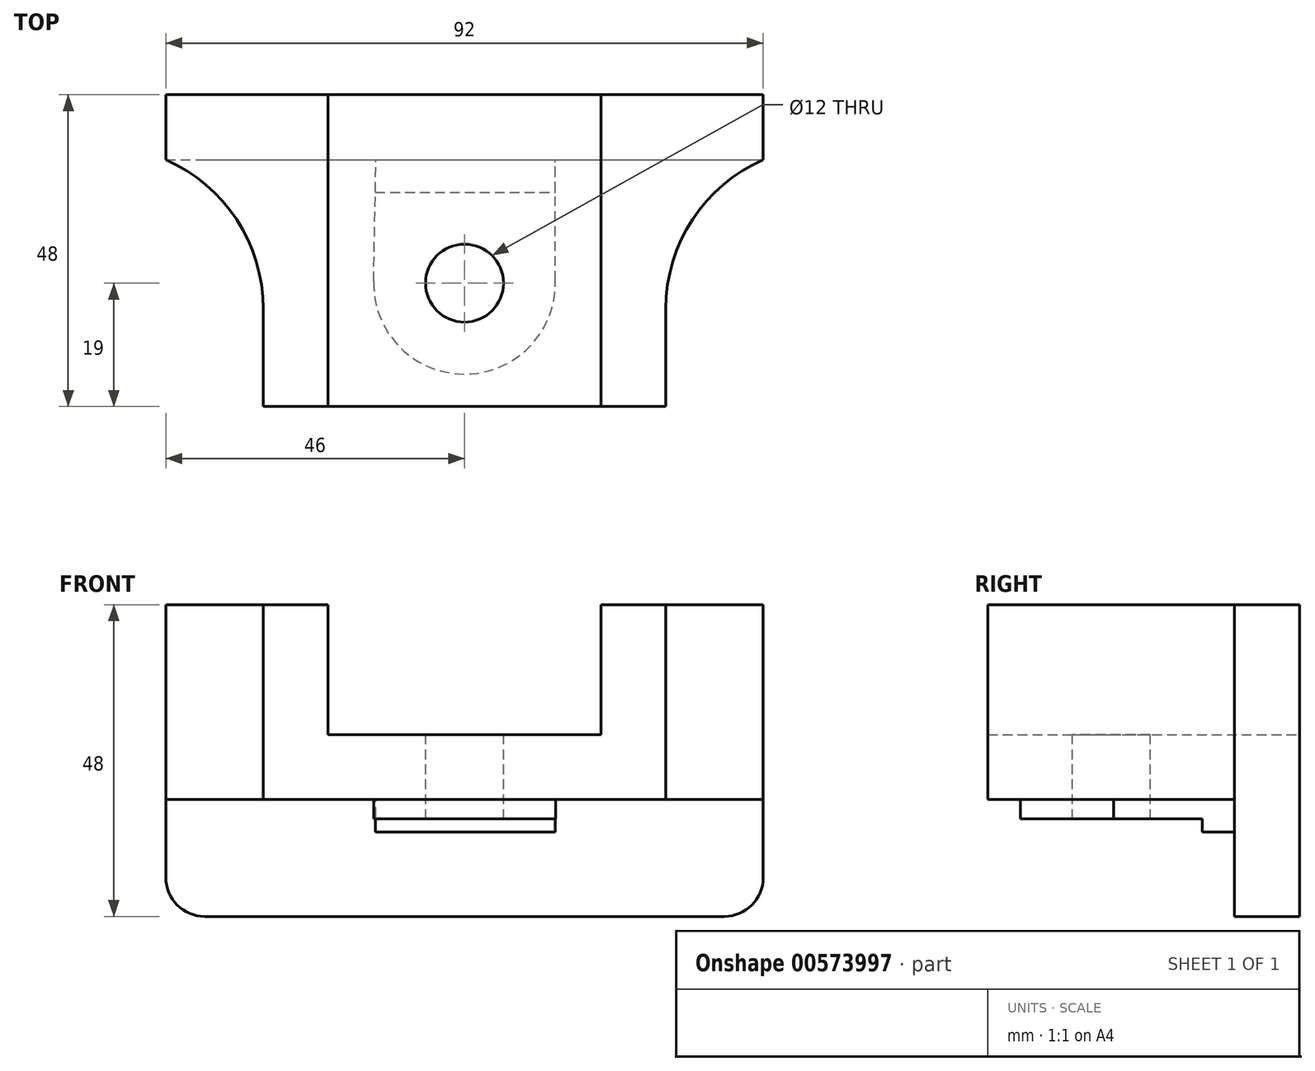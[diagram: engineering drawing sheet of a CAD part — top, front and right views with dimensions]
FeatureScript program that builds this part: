
annotation { "Feature Type Name" : "Feature", "Feature Type Description" : "" }
export const myFeature = defineFeature(function(context is Context, id is Id, definition is map)
    precondition{}
    {
        {
            var Q0;
            Q0=qCreatedBy(makeId("Front.planeOp"),FACE);
            var sketch = newSketch(context, id + "F0", { "sketchPlane" : qUnion([Q0])});
            skLineSegment(sketch, "E0", {"start": v(-46, 0) * mm, "end": v(-46, -42) * mm});
            skLineSegment(sketch, "E1", {"start": v(-40, -48) * mm, "end": v(40, -48) * mm});
            skLineSegment(sketch, "E2", {"start": v(46, -42) * mm, "end": v(46, 0) * mm});
            skLineSegment(sketch, "E3", {"start": v(46, 0) * mm, "end": v(21, 0) * mm});
            skLineSegment(sketch, "E4", {"start": v(21, 0) * mm, "end": v(21, -20) * mm});
            skLineSegment(sketch, "E5", {"start": v(21, -20) * mm, "end": v(-21, -20) * mm});
            skLineSegment(sketch, "E6", {"start": v(-21, -20) * mm, "end": v(-21, 0) * mm});
            skLineSegment(sketch, "E7", {"start": v(-21, 0) * mm, "end": v(-46, 0) * mm});
            skLineSegment(sketch, "E8", {"start": v(-31, 0) * mm, "end": v(-31, -30) * mm});
            skLineSegment(sketch, "E9", {"start": v(-31, -30) * mm, "end": v(31, -30) * mm});
            skLineSegment(sketch, "E10", {"start": v(31, -30) * mm, "end": v(31, 0) * mm});
            skPoint(sketch, "E11.visualSharp", {"position": v(-46, -48) * mm});
            skArc(sketch, "E11.filletArc", {"start": v(-46, -42) * mm, "mid": v(-44.24, -46.24) * mm, "end": v(-40, -48) * mm});
            skPoint(sketch, "E12.visualSharp", {"position": v(46, -48) * mm});
            skArc(sketch, "E12.filletArc", {"start": v(40, -48) * mm, "mid": v(44.24, -46.24) * mm, "end": v(46, -42) * mm});
            skSolve(sketch);
        }
        {
            var Q0;
            {var subQ1=sQuery(id+"F0.wireOp",EDGE,"E4");Q0=makeQuery(id+"F0.imprint","IMPRINT",FACE,{"disambiguationData":[TD([[makeQuery(id+"F0.imprint","IMPRINT",EDGE,{"derivedFrom":subQ1}),1.0]])]});}
            extrude(context, id + "F1", {"entities" : qUnion([Q0]), "depth" : 48 * mm, "offsetDistance" : 25 * mm});
        }
        {
            var Q0;
            Q0 = qSketchRegion(id + "F0", true);
            extrude(context, id + "F2", {"entities" : qUnion([Q0]), "operationType" : NewBodyOperationType.ADD, "depth" : 10 * mm, "offsetDistance" : 25 * mm});
        }
        {
            var Q0;
            Q0=makeQuery(id+"F1.opExtrude","SWEPT_FACE",FACE,{"disambiguationData":[OSD([sQuery(id+"F0.wireOp",EDGE,"E9")])]});
            var sketch = newSketch(context, id + "F3", { "sketchPlane" : qUnion([Q0])});
            skCircle(sketch, "E13", {"center": v(0, 29) * mm, "radius": 6 * mm});
            skArc(sketch, "E14", {"start": v(14, 28.65) * mm, "mid": v(0.04, 43) * mm, "end": v(-14, 28.73) * mm});
            skLineSegment(sketch, "E15", {"start": v(-14, 28.73) * mm, "end": v(-13.64, 10) * mm});
            skLineSegment(sketch, "E16", {"start": v(14, 28.65) * mm, "end": v(14, 10) * mm});
            skLineSegment(sketch, "E17", {"start": v(-13.73, 15) * mm, "end": v(14, 15) * mm});
            skSolve(sketch);
        }
        {
            var Q0;
            Q0=makeQuery(id+"F3.imprint","IMPRINT",FACE,{"disambiguationData":[TD([[makeQuery(id+"F3.imprint","IMPRINT",EDGE,{"derivedFrom":sQuery(id+"F3.wireOp",EDGE,"E13")}),-1.0]])]});
            extrude(context, id + "F4", {"entities" : qUnion([Q0]), "operationType" : NewBodyOperationType.ADD, "depth" : 3 * mm, "offsetDistance" : 25 * mm});
        }
        {
            var Q0;
            {var subQ3=sQuery(id+"F3.wireOp",EDGE,"E17");Q0=makeQuery(id+"F3.imprint","IMPRINT",FACE,{"disambiguationData":[TD([[makeQuery(id+"F3.imprint","IMPRINT",EDGE,{"derivedFrom":subQ3}),-1.0]])]});}
            extrude(context, id + "F5", {"entities" : qUnion([Q0]), "operationType" : NewBodyOperationType.ADD, "depth" : 5 * mm, "offsetDistance" : 25 * mm});
        }
        {
            var Q0;
            Q0=makeQuery(id+"F2.boolean.opBoolean","INTERSECT",EDGE,{"derivedFrom":[makeQuery(id+"F1.opExtrude","SWEPT_FACE",FACE,{"disambiguationData":[OSD([sQuery(id+"F0.wireOp",EDGE,"E10")])]}),makeQuery(id+"F2.opExtrude","CAP_FACE",FACE,{"disambiguationData":[OSD([sQuery(id+"F0.wireOp",EDGE,"E0"),sQuery(id+"F0.wireOp",EDGE,"E1"),sQuery(id+"F0.wireOp",EDGE,"E2"),sQuery(id+"F0.wireOp",EDGE,"E3"),sQuery(id+"F0.wireOp",EDGE,"E4"),sQuery(id+"F0.wireOp",EDGE,"E5"),sQuery(id+"F0.wireOp",EDGE,"E6"),sQuery(id+"F0.wireOp",EDGE,"E7"),sQuery(id+"F0.wireOp",EDGE,"E11.filletArc"),sQuery(id+"F0.wireOp",EDGE,"E12.filletArc")])],"isStart":false})]});
            var Q1;
            Q1=makeQuery(id+"F2.boolean.opBoolean","INTERSECT",EDGE,{"derivedFrom":[makeQuery(id+"F1.opExtrude","SWEPT_FACE",FACE,{"disambiguationData":[OSD([sQuery(id+"F0.wireOp",EDGE,"E8")])]}),makeQuery(id+"F2.opExtrude","CAP_FACE",FACE,{"disambiguationData":[OSD([sQuery(id+"F0.wireOp",EDGE,"E0"),sQuery(id+"F0.wireOp",EDGE,"E1"),sQuery(id+"F0.wireOp",EDGE,"E2"),sQuery(id+"F0.wireOp",EDGE,"E3"),sQuery(id+"F0.wireOp",EDGE,"E4"),sQuery(id+"F0.wireOp",EDGE,"E5"),sQuery(id+"F0.wireOp",EDGE,"E6"),sQuery(id+"F0.wireOp",EDGE,"E7"),sQuery(id+"F0.wireOp",EDGE,"E11.filletArc"),sQuery(id+"F0.wireOp",EDGE,"E12.filletArc")])],"isStart":false})]});
            fillet(context, id + "F6", {"entities" : qUnion([Q0, Q1]), "radius" : 25 * mm, "tangentPropagation" : true, "allowEdgeOverflow" : false});
        }
        {
            var Q0;
            Q0=sQuery(id+"F3.wireOp",VERTEX,"E13.center");
            var Q1;
            Q1=makeQuery(id+"F1.opExtrude","SWEPT_BODY",BODY,{"disambiguationData":[OSD([sQuery(id+"F0.wireOp",EDGE,"E3"),sQuery(id+"F0.wireOp",EDGE,"E4"),sQuery(id+"F0.wireOp",EDGE,"E5"),sQuery(id+"F0.wireOp",EDGE,"E6"),sQuery(id+"F0.wireOp",EDGE,"E7"),sQuery(id+"F0.wireOp",EDGE,"E8"),sQuery(id+"F0.wireOp",EDGE,"E9"),sQuery(id+"F0.wireOp",EDGE,"E10")])]});
            hole(context, id + "F7", {"style" : HoleStyle.SIMPLE, "endStyle" : HoleEndStyle.THROUGH, "holeDiameter" : 12 * mm, "isTappedThrough" : true, "tappedDepth" : 12 * mm, "tapClearance" : 3, "locations" : qUnion([Q0]), "scope" : qUnion([Q1])});
        }
    });
